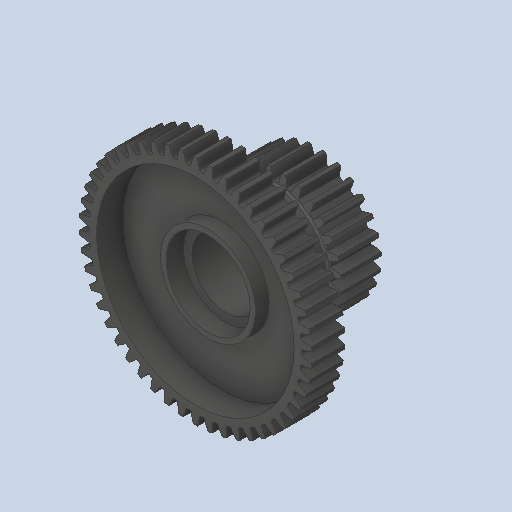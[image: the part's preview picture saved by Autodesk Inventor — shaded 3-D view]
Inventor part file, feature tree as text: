
AUTODESK INVENTOR PART (.ipt)
format: ipt  version: 2023 (Build 270158000, 158)  size: 579,072 bytes
history: native  units: in
note: dims shown in document units (in); Inventor stores cm internally (conversion verified against a paired STEP export)
features: chamfer x1
ambient origin geometry x8: Origin, YZ Plane, XZ Plane, XY Plane, X Axis, Y Axis, Z Axis, Center Point
bodies: Solid1 (feature_tree)
feature tree (1):
  chamfer  "Chamfer2"  [1 undecoded]
note: 1 required parameter value undecoded (feature->parameter linkage not recoverable at this tier; creation-order binding heuristic only, values carry confidence <= 0.55)
